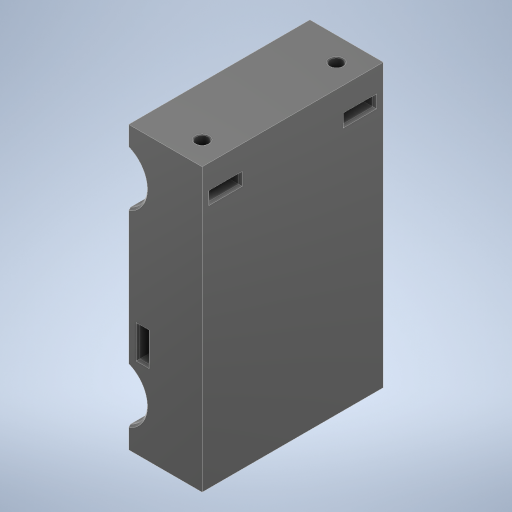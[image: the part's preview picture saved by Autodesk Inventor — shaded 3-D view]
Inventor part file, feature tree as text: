
AUTODESK INVENTOR PART (.ipt)
format: ipt  version: 2023 (Build 270158000, 158)  size: 522,240 bytes
history: native  units: in
note: dims shown in document units (in); Inventor stores cm internally (conversion verified against a paired STEP export)
features: sketch x6, extrude x4, chamfer x3, plane x3, hole x2, fillet x1, mirror x1
ambient origin geometry x8: Origin, YZ Plane, XZ Plane, XY Plane, X Axis, Y Axis, Z Axis, Center Point
bodies: Solid1 (feature_tree)
feature tree (20):
  extrude  "Extrusion1"  Depth=0.5956in
  chamfer  "Chamfer1"  [1 undecoded]
  plane  "Work Plane1"
  plane  "Work Plane2"
  extrude  "Extrusion3"  Depth=0.0984in TaperAngle=0.0deg
  hole  "Hole1"  [1 undecoded]
  extrude  "Extrusion4"  Depth=0.0984in TaperAngle=0.0deg
  fillet  "Fillet1"  Radius=3.937in
  chamfer  "Chamfer2"  Distance=0.2096in
  hole  "Hole2"  [1 undecoded]
  extrude  "Extrusion5"  Depth=0.0984in
  plane  "Work Plane3"
  mirror  "Mirror2"
  chamfer  "Chamfer3"  Distance=0.25in
  sketch  "Sketch1"  dims[d0=3.0in d1=0.5956in]
  sketch  "Sketch4"  dims[d2=0.5956in]
  sketch  "Sketch5"  dims[d3=1.8in]
  sketch  "Sketch6"  dims[d4=0.5in]
  sketch  "Sketch7"  dims[d5=2.0in]
  sketch  "Sketch8"  dims[d7=0.5in d8=0.0in d9=1.9291in d10=0.0in d11=0.02in d12=0.125in d13=45.0deg d25=0.0in d26=0.1181in d27=3.937in d28=0.0in d29=0.2096in d30=0.25in d31=0.25in d32=0.25in d33=0.25in d34=0.1339in d35=0.2953in d36=0.2559in d37=0.1181in d38=90.0deg d39=0.3937in d40=0.8108in d41=0.0984in d42=0.2756in d43=0.315in d44=0.5256in d45=0.0in d46=0.0079in d47=0.0197in d48=0.0492in d49=45.0deg d50=0.1969in d51=0.1969in d52=1.035in d53=1.035in d54=0.1339in d55=0.2953in d56=0.2559in d57=0.7087in d58=0.5635in d59=0.2953in d60=0.8108in d61=0.315in d62=0.0984in d63=0.0984in d64=0.5256in d65=0.0in d66=0.963in d67=0.0197in d68=0.0492in d69=45.0deg]
note: 3 required parameter values undecoded (feature->parameter linkage not recoverable at this tier; creation-order binding heuristic only, values carry confidence <= 0.55)
